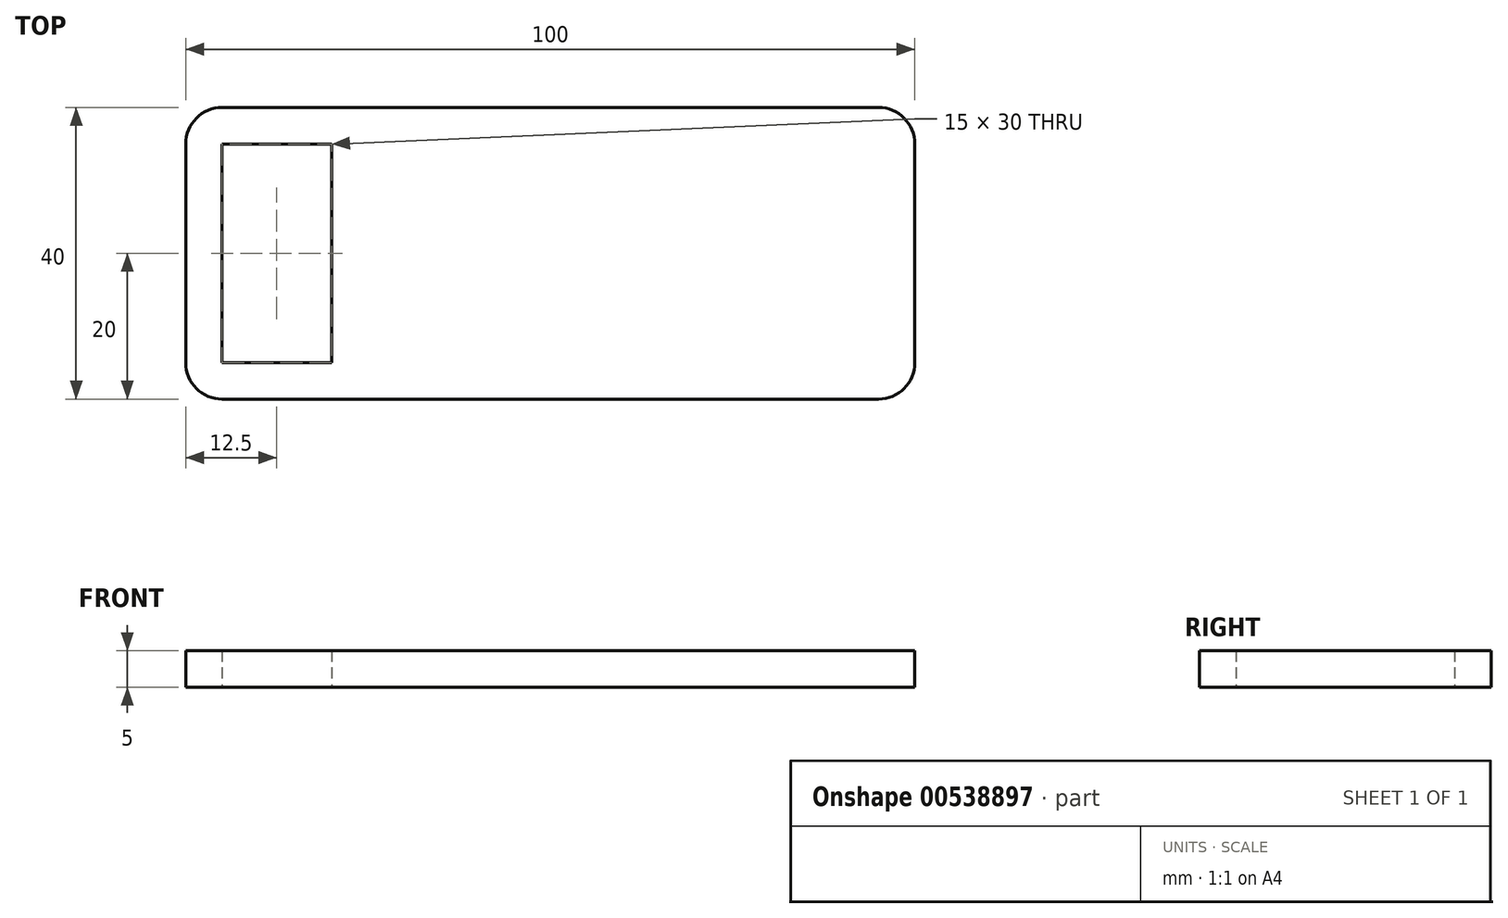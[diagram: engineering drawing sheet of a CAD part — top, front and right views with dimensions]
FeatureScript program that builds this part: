
annotation { "Feature Type Name" : "Feature", "Feature Type Description" : "" }
export const myFeature = defineFeature(function(context is Context, id is Id, definition is map)
    precondition{}
    {
        {
            var Q0;
            Q0=qCreatedBy(makeId("Top.planeOp"),FACE);
            var sketch = newSketch(context, id + "F0", { "sketchPlane" : qUnion([Q0])});
            skLineSegment(sketch, "E0.bottom", {"start": v(50, -20) * mm, "end": v(-50, -20) * mm});
            skLineSegment(sketch, "E0.top", {"start": v(50, 20) * mm, "end": v(-50, 20) * mm});
            skLineSegment(sketch, "E0.left", {"start": v(50, -20) * mm, "end": v(50, 20) * mm});
            skLineSegment(sketch, "E0.right", {"start": v(-50, -20) * mm, "end": v(-50, 20) * mm});
            skPoint(sketch, "E0.middle", {"position": v(0, 0) * mm});
            skLineSegment(sketch, "E1.bottom", {"start": v(-30, 15) * mm, "end": v(-45, 15) * mm});
            skLineSegment(sketch, "E1.top", {"start": v(-30, -15) * mm, "end": v(-45, -15) * mm});
            skLineSegment(sketch, "E1.left", {"start": v(-30, 15) * mm, "end": v(-30, -15) * mm});
            skLineSegment(sketch, "E1.right", {"start": v(-45, 15) * mm, "end": v(-45, -15) * mm});
            skPoint(sketch, "E1.middle", {"position": v(-37.5, 0) * mm});
            skSolve(sketch);
        }
        {
            var Q0;
            Q0=qSketchRegion(id+"F0",true);
            extrude(context, id + "F1", {"entities" : qUnion([Q0]), "depth" : 5 * mm});
        }
        {
            var Q0;
            Q0=makeQuery(id+"F1.opExtrude","SWEPT_EDGE",EDGE,{"disambiguationData":[OSD([sQuery(id+"F0.wireOp",EDGE,"E0.bottom"),sQuery(id+"F0.wireOp",EDGE,"E0.right")])]});
            var Q1;
            Q1=makeQuery(id+"F1.opExtrude","SWEPT_EDGE",EDGE,{"disambiguationData":[OSD([sQuery(id+"F0.wireOp",EDGE,"E0.bottom"),sQuery(id+"F0.wireOp",EDGE,"E0.left")])]});
            var Q2;
            Q2=makeQuery(id+"F1.opExtrude","SWEPT_EDGE",EDGE,{"disambiguationData":[OSD([sQuery(id+"F0.wireOp",EDGE,"E0.top"),sQuery(id+"F0.wireOp",EDGE,"E0.left")])]});
            var Q3;
            Q3=makeQuery(id+"F1.opExtrude","SWEPT_EDGE",EDGE,{"disambiguationData":[OSD([sQuery(id+"F0.wireOp",EDGE,"E0.top"),sQuery(id+"F0.wireOp",EDGE,"E0.right")])]});
            fillet(context, id + "F2", {"entities" : qUnion([Q0, Q1, Q2, Q3]), "radius" : 5 * mm, "tangentPropagation" : true, "allowEdgeOverflow" : false});
        }
    });
